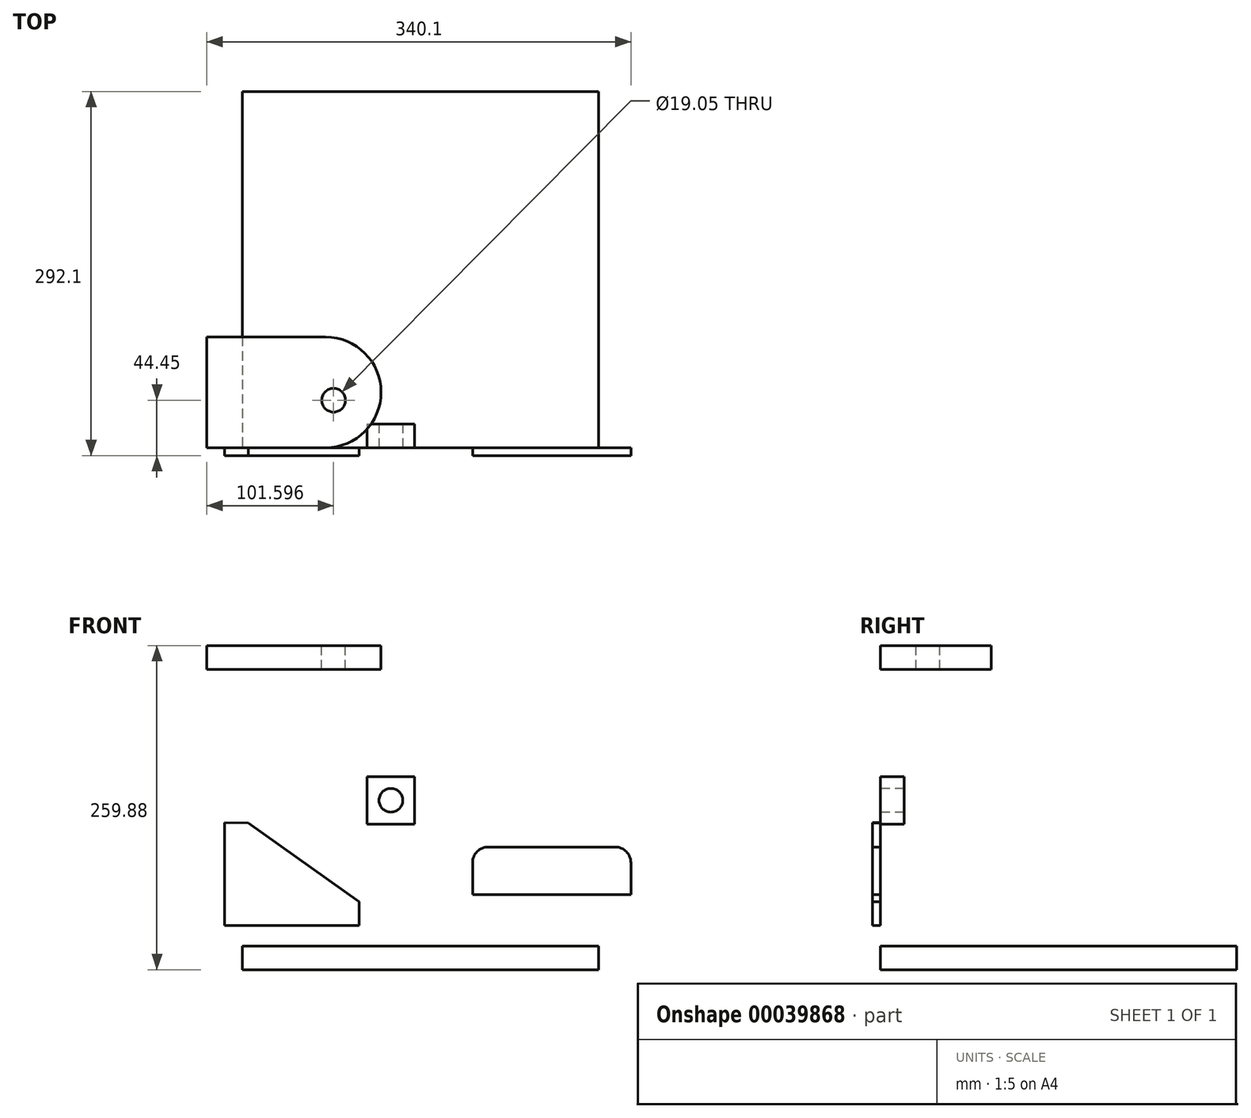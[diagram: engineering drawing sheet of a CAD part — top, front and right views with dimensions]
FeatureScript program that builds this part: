
annotation { "Feature Type Name" : "Feature", "Feature Type Description" : "" }
export const myFeature = defineFeature(function(context is Context, id is Id, definition is map)
    precondition{}
    {
        {
            var Q0;
            Q0=qCreatedBy(makeId("Front.planeOp"),FACE);
            var sketch = newSketch(context, id + "F0", { "sketchPlane" : qUnion([Q0])});
            skLineSegment(sketch, "E0", {"start": v(-70.96, 45.85) * mm, "end": v(-70.96, -36.7) * mm});
            skLineSegment(sketch, "E1", {"start": v(-70.96, -36.7) * mm, "end": v(36.99, -36.7) * mm});
            skLineSegment(sketch, "E2", {"start": v(36.99, -36.7) * mm, "end": v(36.99, -17.65) * mm});
            skLineSegment(sketch, "E3", {"start": v(36.99, -17.65) * mm, "end": v(-51.91, 45.51) * mm});
            skLineSegment(sketch, "E4", {"start": v(-51.91, 45.51) * mm, "end": v(-70.96, 45.85) * mm});
            skLineSegment(sketch, "E5", {"start": v(127.99, 13.63) * mm, "end": v(127.99, -11.77) * mm});
            skLineSegment(sketch, "E6", {"start": v(127.99, -11.77) * mm, "end": v(254.99, -11.77) * mm});
            skLineSegment(sketch, "E7", {"start": v(254.99, -11.77) * mm, "end": v(254.99, 13.63) * mm});
            skLineSegment(sketch, "E8", {"start": v(242.29, 26.33) * mm, "end": v(140.69, 26.33) * mm});
            skPoint(sketch, "E9.visualSharp", {"position": v(127.99, 26.33) * mm});
            skArc(sketch, "E9.filletArc", {"start": v(140.69, 26.33) * mm, "mid": v(131.7, 22.6) * mm, "end": v(127.99, 13.63) * mm});
            skPoint(sketch, "E10.visualSharp", {"position": v(254.99, 26.33) * mm});
            skArc(sketch, "E10.filletArc", {"start": v(254.99, 13.63) * mm, "mid": v(251.27, 22.6) * mm, "end": v(242.29, 26.33) * mm});
            skSolve(sketch);
        }
        {
            var Q0;
            Q0=makeQuery(id+"F0.imprint","IMPRINT",FACE,{"disambiguationData":[TD([[makeQuery(id+"F0.imprint","IMPRINT",EDGE,{"derivedFrom":sQuery(id+"F0.wireOp",EDGE,"E0")}),1.0]])]});
            var Q1;
            Q1=makeQuery(id+"F0.imprint","IMPRINT",FACE,{"disambiguationData":[TD([[makeQuery(id+"F0.imprint","IMPRINT",EDGE,{"derivedFrom":sQuery(id+"F0.wireOp",EDGE,"E5")}),1.0]])]});
            extrude(context, id + "F1", {"entities" : qUnion([Q0, Q1]), "depth" : 6.35 * mm});
        }
        {
            var Q0;
            Q0=qCreatedBy(makeId("Front.planeOp"),FACE);
            var sketch = newSketch(context, id + "F2", { "sketchPlane" : qUnion([Q0])});
            skLineSegment(sketch, "E11.bottom", {"start": v(-56.7, -53.08) * mm, "end": v(229.04, -53.08) * mm});
            skLineSegment(sketch, "E11.top", {"start": v(-56.7, -72.13) * mm, "end": v(229.04, -72.13) * mm});
            skLineSegment(sketch, "E11.left", {"start": v(-56.7, -53.08) * mm, "end": v(-56.7, -72.13) * mm});
            skLineSegment(sketch, "E11.right", {"start": v(229.04, -53.08) * mm, "end": v(229.04, -72.13) * mm});
            skSolve(sketch);
        }
        {
            var Q0;
            Q0=makeQuery(id+"F2.imprint","IMPRINT",FACE,{"disambiguationData":[TD([[makeQuery(id+"F2.imprint","IMPRINT",EDGE,{"derivedFrom":sQuery(id+"F2.wireOp",EDGE,"E11.bottom")}),-1.0]])]});
            extrude(context, id + "F3", {"entities" : qUnion([Q0]), "oppositeDirection" : true, "depth" : 285.75 * mm});
        }
        {
            var Q0;
            Q0=qCreatedBy(makeId("Front.planeOp"),FACE);
            var sketch = newSketch(context, id + "F4", { "sketchPlane" : qUnion([Q0])});
            skLineSegment(sketch, "E12.bottom", {"start": v(43.23, 82.8) * mm, "end": v(81.33, 82.8) * mm});
            skLineSegment(sketch, "E12.top", {"start": v(43.23, 44.7) * mm, "end": v(81.33, 44.7) * mm});
            skLineSegment(sketch, "E12.left", {"start": v(43.23, 82.8) * mm, "end": v(43.23, 44.7) * mm});
            skLineSegment(sketch, "E12.right", {"start": v(81.33, 82.8) * mm, "end": v(81.33, 44.7) * mm});
            skCircle(sketch, "E13", {"center": v(62.49, 63.75) * mm, "radius": 9.53 * mm});
            skPoint(sketch, "E13.centerSnap0", {"position": v(43.23, 63.75) * mm});
            skSolve(sketch);
        }
        {
            var Q0;
            Q0=makeQuery(id+"F4.imprint","IMPRINT",FACE,{"disambiguationData":[TD([[makeQuery(id+"F4.imprint","IMPRINT",EDGE,{"derivedFrom":sQuery(id+"F4.wireOp",EDGE,"E12.bottom")}),-1.0]])]});
            extrude(context, id + "F5", {"entities" : qUnion([Q0]), "oppositeDirection" : true, "depth" : 19.05 * mm});
        }
        {
            var Q0;
            Q0=qCreatedBy(makeId("Front.planeOp"),FACE);
            var sketch = newSketch(context, id + "F6", { "sketchPlane" : qUnion([Q0])});
            skLineSegment(sketch, "E14.rect.bottom", {"start": v(-85.11, 168.7) * mm, "end": v(54.59, 168.7) * mm});
            skLineSegment(sketch, "E14.rect.top", {"start": v(-85.11, 187.75) * mm, "end": v(54.59, 187.75) * mm});
            skLineSegment(sketch, "E14.rect.left", {"start": v(-85.11, 168.7) * mm, "end": v(-85.11, 187.75) * mm});
            skLineSegment(sketch, "E14.rect.right", {"start": v(54.59, 168.7) * mm, "end": v(54.59, 187.75) * mm});
            skPoint(sketch, "E14.rect.middle", {"position": v(-15.26, 178.23) * mm});
            skSolve(sketch);
        }
        {
            var Q0;
            Q0 = qSketchRegion(id + "F6", true);
            extrude(context, id + "F7", {"entities" : qUnion([Q0]), "oppositeDirection" : true, "depth" : 88.9 * mm});
        }
        {
            var Q0;
            Q0=makeQuery(id+"F7.opExtrude","SWEPT_FACE",FACE,{"disambiguationData":[OSD([sQuery(id+"F6.wireOp",EDGE,"E14.rect.top")])]});
            var sketch = newSketch(context, id + "F8", { "sketchPlane" : qUnion([Q0])});
            skCircle(sketch, "E15", {"center": v(16.49, 38.1) * mm, "radius": 9.53 * mm});
            skSolve(sketch);
        }
        {
            var Q0;
            Q0 = qSketchRegion(id + "F8", true);
            extrude(context, id + "F9", {"entities" : qUnion([Q0]), "operationType" : NewBodyOperationType.REMOVE, "oppositeDirection" : true, "depth" : 76.2 * mm});
        }
        {
            var Q0;
            Q0=makeQuery(id+"F7.opExtrude","CAP_EDGE",EDGE,{"disambiguationData":[OSD([sQuery(id+"F6.wireOp",EDGE,"E14.rect.right")])],"isStart":true});
            var Q1;
            Q1=makeQuery(id+"F7.opExtrude","CAP_EDGE",EDGE,{"disambiguationData":[OSD([sQuery(id+"F6.wireOp",EDGE,"E14.rect.right")])],"isStart":false});
            fillet(context, id + "F10", {"entities" : qUnion([Q0, Q1]), "radius" : 44.45 * mm, "tangentPropagation" : true, "allowEdgeOverflow" : false});
        }
    });
